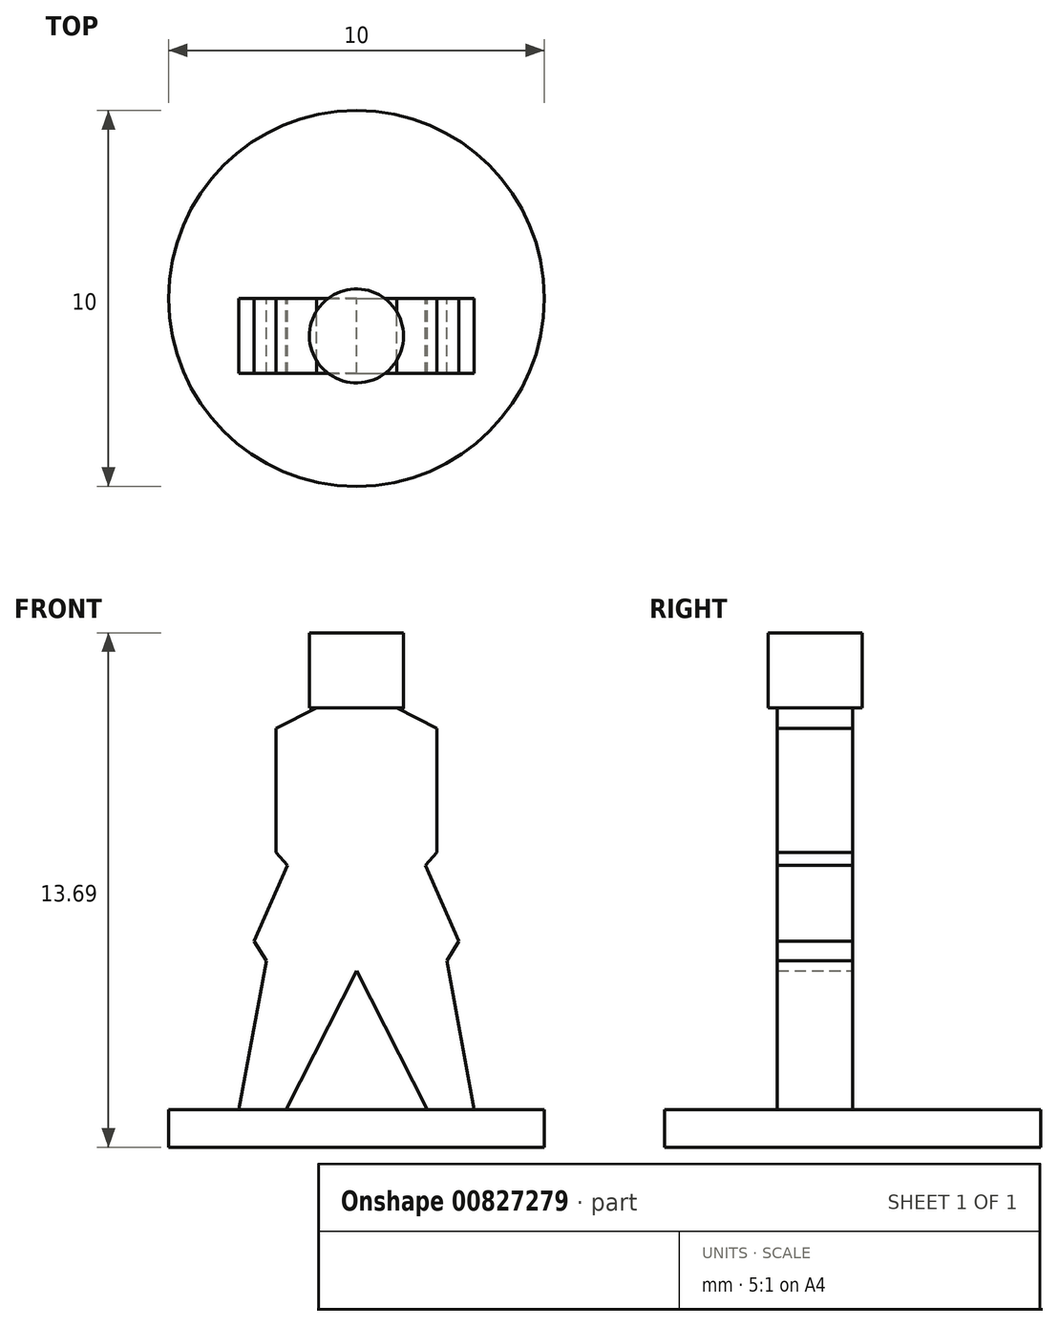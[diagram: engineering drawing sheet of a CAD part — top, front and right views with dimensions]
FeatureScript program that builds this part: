
annotation { "Feature Type Name" : "Feature", "Feature Type Description" : "" }
export const myFeature = defineFeature(function(context is Context, id is Id, definition is map)
    precondition{}
    {
        {
            var Q0;
            Q0=qCreatedBy(makeId("Top.planeOp"),FACE);
            var sketch = newSketch(context, id + "F0", { "sketchPlane" : qUnion([Q0])});
            skCircle(sketch, "E0", {"center": v(0, 0) * mm, "radius": 5 * mm});
            skSolve(sketch);
        }
        {
            var Q0;
            Q0=makeQuery(id+"F0.imprint","IMPRINT",FACE,{"disambiguationData":[TD([[makeQuery(id+"F0.imprint","IMPRINT",EDGE,{"derivedFrom":sQuery(id+"F0.wireOp",EDGE,"E0")}),1.0]])]});
            extrude(context, id + "F1", {"entities" : qUnion([Q0]), "depth" : 1 * mm, "offsetDistance" : 25 * mm});
        }
        {
            var Q0;
            Q0=qCreatedBy(makeId("Front.planeOp"),FACE);
            var sketch = newSketch(context, id + "F2", { "sketchPlane" : qUnion([Q0])});
            skLineSegment(sketch, "E1", {"start": v(-3.17, 0.8) * mm, "end": v(-2.4, 4.96) * mm});
            skLineSegment(sketch, "E2", {"start": v(-2.4, 4.96) * mm, "end": v(-2.72, 5.48) * mm});
            skLineSegment(sketch, "E3", {"start": v(-2.72, 5.48) * mm, "end": v(-1.83, 7.5) * mm});
            skLineSegment(sketch, "E4", {"start": v(-1.83, 7.5) * mm, "end": v(-2.14, 7.85) * mm});
            skLineSegment(sketch, "E5", {"start": v(-2.14, 7.85) * mm, "end": v(-2.14, 11.14) * mm});
            skLineSegment(sketch, "E6", {"start": v(-2.14, 11.14) * mm, "end": v(-1.07, 11.69) * mm});
            skLineSegment(sketch, "E7", {"start": v(-1.07, 11.69) * mm, "end": v(0, 11.69) * mm});
            skLineSegment(sketch, "E8", {"start": v(0, 11.69) * mm, "end": v(0, 4.7) * mm});
            skLineSegment(sketch, "E9", {"start": v(0, 4.7) * mm, "end": v(0, 4.7) * mm});
            skLineSegment(sketch, "E10", {"start": v(0, 4.7) * mm, "end": v(-2.02, 0.73) * mm});
            skLineSegment(sketch, "E11", {"start": v(-2.02, 0.73) * mm, "end": v(-3.17, 0.8) * mm});
            skLineSegment(sketch, "E12.MirrorCS", {"start": v(1.83, 7.5) * mm, "end": v(2.14, 7.85) * mm});
            skLineSegment(sketch, "E13.MirrorCS", {"start": v(2.4, 4.96) * mm, "end": v(2.72, 5.48) * mm});
            skLineSegment(sketch, "E14.MirrorCS", {"start": v(1.07, 11.69) * mm, "end": v(0, 11.69) * mm});
            skLineSegment(sketch, "E15.MirrorCS", {"start": v(2.14, 11.14) * mm, "end": v(1.07, 11.69) * mm});
            skLineSegment(sketch, "E16.MirrorCS", {"start": v(2.14, 7.85) * mm, "end": v(2.14, 11.14) * mm});
            skLineSegment(sketch, "E17.MirrorCS", {"start": v(0, 4.7) * mm, "end": v(2.02, 0.73) * mm});
            skLineSegment(sketch, "E18.MirrorCS", {"start": v(2.72, 5.48) * mm, "end": v(1.83, 7.5) * mm});
            skLineSegment(sketch, "E19.MirrorCS", {"start": v(2.02, 0.73) * mm, "end": v(3.17, 0.8) * mm});
            skLineSegment(sketch, "E20.MirrorCS", {"start": v(3.17, 0.8) * mm, "end": v(2.4, 4.96) * mm});
            skSolve(sketch);
        }
        {
            var Q0;
            Q0=makeQuery(id+"F2.imprint","IMPRINT",FACE,{"disambiguationData":[TD([[makeQuery(id+"F2.imprint","IMPRINT",EDGE,{"derivedFrom":sQuery(id+"F2.wireOp",EDGE,"E1")}),-1.0]])]});
            var Q1;
            Q1=makeQuery(id+"F2.imprint","IMPRINT",FACE,{"disambiguationData":[TD([[makeQuery(id+"F2.imprint","IMPRINT",EDGE,{"derivedFrom":sQuery(id+"F2.wireOp",EDGE,"E8")}),1.0]])]});
            extrude(context, id + "F3", {"entities" : qUnion([Q0, Q1]), "operationType" : NewBodyOperationType.ADD, "depth" : 2 * mm, "offsetDistance" : 25 * mm});
        }
        {
            var Q0;
            Q0=makeQuery(id+"F3.opExtrude","SWEPT_FACE",FACE,{"disambiguationData":[OSD([sQuery(id+"F2.wireOp",EDGE,"E7"),sQuery(id+"F2.wireOp",EDGE,"E14.MirrorCS")])]});
            var sketch = newSketch(context, id + "F4", { "sketchPlane" : qUnion([Q0])});
            skLineSegment(sketch, "E21", {"start": v(0, 0) * mm, "end": v(0, -2) * mm});
            skCircle(sketch, "E22", {"center": v(0, -1) * mm, "radius": 1.25 * mm});
            skSolve(sketch);
        }
        {
            var Q0;
            {var subQ0=sQuery(id+"F4.wireOp",EDGE,"E22");var subQ1=makeQuery(id+"F3.opExtrude","CAP_EDGE",EDGE,{"disambiguationData":[OSD([sQuery(id+"F2.wireOp",EDGE,"E7"),sQuery(id+"F2.wireOp",EDGE,"E14.MirrorCS")])],"isStart":true});var subQ2=makeQuery(id+"F4.imprint","INTERSECT",VERTEX,{"disambiguationData":[OD(0.0)],"derivedFrom":[subQ1,subQ0]});Q0=makeQuery(id+"F4.imprint","IMPRINT",FACE,{"disambiguationData":[TD([[makeQuery(id+"F4.imprint","IMPRINT",EDGE,{"disambiguationData":[TD([[subQ2,-1.0]])],"derivedFrom":subQ0}),1.0]])]});}
            var Q1;
            {var subQ0=sQuery(id+"F4.wireOp",EDGE,"E22");var subQ1=makeQuery(id+"F3.opExtrude","SWEPT_EDGE",EDGE,{"disambiguationData":[OSD([sQuery(id+"F2.wireOp",EDGE,"E14.MirrorCS"),sQuery(id+"F2.wireOp",EDGE,"E15.MirrorCS")])]});var subQ2=makeQuery(id+"F4.imprint","INTERSECT",VERTEX,{"disambiguationData":[OD(0.0)],"derivedFrom":[subQ1,subQ0]});Q1=makeQuery(id+"F4.imprint","IMPRINT",FACE,{"disambiguationData":[TD([[makeQuery(id+"F4.imprint","IMPRINT",EDGE,{"disambiguationData":[TD([[subQ2,1.0]])],"derivedFrom":subQ0}),1.0]])]});}
            var Q2;
            {var subQ10=sQuery(id+"F4.wireOp",EDGE,"E21");Q2=makeQuery(id+"F4.imprint","IMPRINT",FACE,{"disambiguationData":[TD([[makeQuery(id+"F4.imprint","IMPRINT",EDGE,{"derivedFrom":subQ10}),1.0]])]});}
            var Q3;
            {var subQ0=sQuery(id+"F4.wireOp",EDGE,"E22");var subQ1=makeQuery(id+"F3.opExtrude","CAP_EDGE",EDGE,{"disambiguationData":[OSD([sQuery(id+"F2.wireOp",EDGE,"E7"),sQuery(id+"F2.wireOp",EDGE,"E14.MirrorCS")])],"isStart":false});var subQ2=makeQuery(id+"F4.imprint","INTERSECT",VERTEX,{"disambiguationData":[OD(0.0)],"derivedFrom":[subQ1,subQ0]});Q3=makeQuery(id+"F4.imprint","IMPRINT",FACE,{"disambiguationData":[TD([[makeQuery(id+"F4.imprint","IMPRINT",EDGE,{"disambiguationData":[TD([[subQ2,-1.0]])],"derivedFrom":subQ0}),1.0]])]});}
            var Q4;
            {var subQ5=sQuery(id+"F4.wireOp",EDGE,"E21");Q4=makeQuery(id+"F4.imprint","IMPRINT",FACE,{"disambiguationData":[TD([[makeQuery(id+"F4.imprint","IMPRINT",EDGE,{"derivedFrom":subQ5}),-1.0]])]});}
            var Q5;
            {var subQ0=sQuery(id+"F4.wireOp",EDGE,"E22");var subQ1=makeQuery(id+"F3.opExtrude","SWEPT_EDGE",EDGE,{"disambiguationData":[OSD([sQuery(id+"F2.wireOp",EDGE,"E6"),sQuery(id+"F2.wireOp",EDGE,"E7")])]});var subQ2=makeQuery(id+"F4.imprint","INTERSECT",VERTEX,{"disambiguationData":[OD(0.0)],"derivedFrom":[subQ1,subQ0]});Q5=makeQuery(id+"F4.imprint","IMPRINT",FACE,{"disambiguationData":[TD([[makeQuery(id+"F4.imprint","IMPRINT",EDGE,{"disambiguationData":[TD([[subQ2,-1.0]])],"derivedFrom":subQ0}),1.0]])]});}
            extrude(context, id + "F5", {"entities" : qUnion([Q0, Q1, Q2, Q3, Q4, Q5]), "operationType" : NewBodyOperationType.ADD, "depth" : 2 * mm, "offsetDistance" : 25 * mm});
        }
    });
